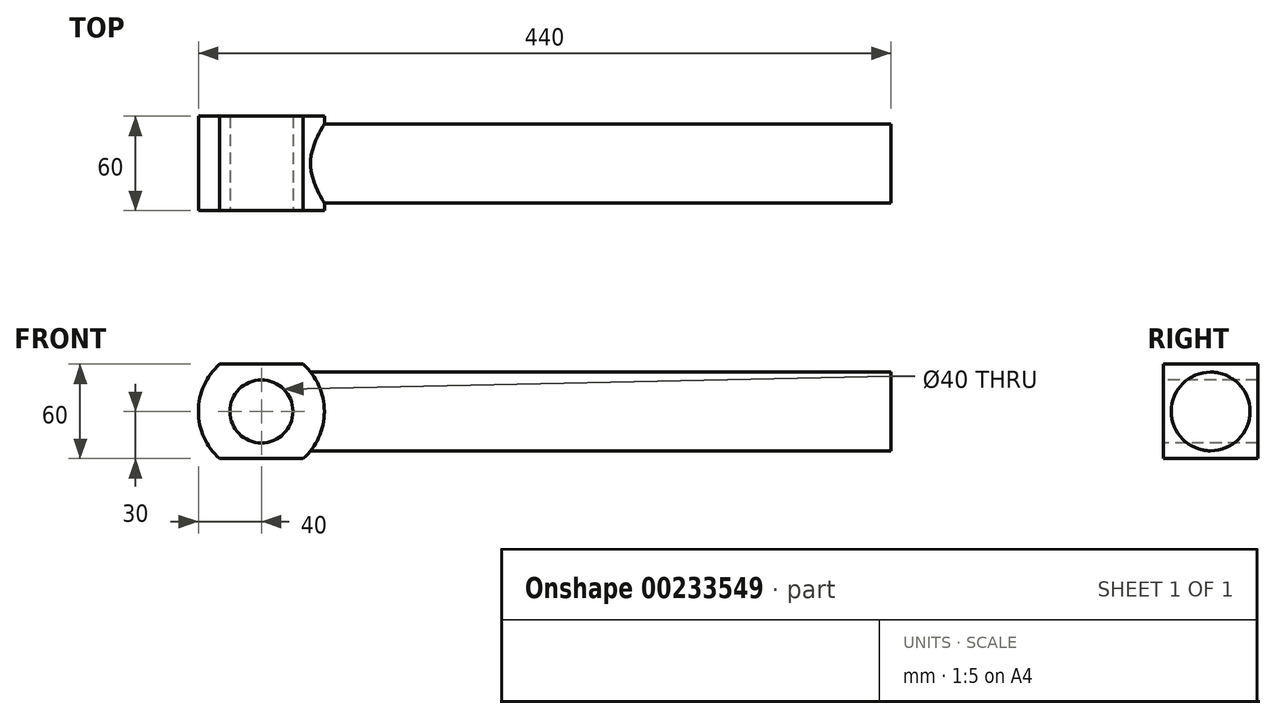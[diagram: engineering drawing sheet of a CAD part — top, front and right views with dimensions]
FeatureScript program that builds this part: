
annotation { "Feature Type Name" : "Feature", "Feature Type Description" : "" }
export const myFeature = defineFeature(function(context is Context, id is Id, definition is map)
    precondition{}
    {
        {
            var Q0;
            Q0=qCreatedBy(makeId("Front.planeOp"),FACE);
            var sketch = newSketch(context, id + "F0", { "sketchPlane" : qUnion([Q0])});
            skLineSegment(sketch, "E0", {"start": v(0, 0) * mm, "end": v(0, 25) * mm});
            skLineSegment(sketch, "E1", {"start": v(0, 25) * mm, "end": v(400, 25) * mm});
            skLineSegment(sketch, "E2", {"start": v(400, 25) * mm, "end": v(400, 0) * mm});
            skLineSegment(sketch, "E3", {"start": v(400, 0) * mm, "end": v(0, 0) * mm});
            skSolve(sketch);
        }
        {
            var Q0;
            Q0=makeQuery(id+"F0.imprint","IMPRINT",FACE,{"disambiguationData":[TD([[makeQuery(id+"F0.imprint","IMPRINT",EDGE,{"derivedFrom":sQuery(id+"F0.wireOp",EDGE,"E0")}),-1.0]])]});
            var Q1;
            Q1=sQuery(id+"F0.wireOp",EDGE,"E3");
            revolve(context, id + "F1", {"entities" : qUnion([Q0]), "axis" : qUnion([Q1]), "revolveType" : RevolveType.FULL});
        }
        {
            var Q0;
            Q0=qCreatedBy(makeId("Front.planeOp"),FACE);
            var sketch = newSketch(context, id + "F2", { "sketchPlane" : qUnion([Q0])});
            skArc(sketch, "E4", {"start": v(-26.46, 30) * mm, "mid": v(-40, 0) * mm, "end": v(-26.46, -30) * mm});
            skLineSegment(sketch, "E5.bottom", {"start": v(26.46, 30) * mm, "end": v(-26.46, 30) * mm});
            skLineSegment(sketch, "E5.top", {"start": v(26.46, -30) * mm, "end": v(-26.46, -30) * mm});
            skArc(sketch, "E6.trimOffspring", {"start": v(26.46, -30) * mm, "mid": v(40, 0) * mm, "end": v(26.46, 30) * mm});
            skCircle(sketch, "E7", {"center": v(0, 0) * mm, "radius": 20 * mm});
            skSolve(sketch);
        }
        {
            var Q0;
            Q0=makeQuery(id+"F2.imprint","IMPRINT",FACE,{"disambiguationData":[TD([[makeQuery(id+"F2.imprint","IMPRINT",EDGE,{"derivedFrom":sQuery(id+"F2.wireOp",EDGE,"E4")}),1.0]])]});
            var Q1;
            Q1=makeQuery(id+"F2.imprint","IMPRINT",FACE,{"disambiguationData":[TD([[makeQuery(id+"F2.imprint","IMPRINT",EDGE,{"derivedFrom":sQuery(id+"F2.wireOp",EDGE,"E7")}),1.0]])]});
            extrude(context, id + "F3", {"entities" : qUnion([Q0, Q1]), "operationType" : NewBodyOperationType.ADD, "endBound" : BoundingType.SYMMETRIC, "depth" : 60 * mm});
        }
        {
            var Q0;
            Q0=makeQuery(id+"F2.imprint","IMPRINT",FACE,{"disambiguationData":[TD([[makeQuery(id+"F2.imprint","IMPRINT",EDGE,{"derivedFrom":sQuery(id+"F2.wireOp",EDGE,"E7")}),1.0]])]});
            extrude(context, id + "F4", {"entities" : qUnion([Q0]), "operationType" : NewBodyOperationType.REMOVE, "endBound" : BoundingType.SYMMETRIC, "oppositeDirection" : true, "depth" : 60 * mm});
        }
    });
